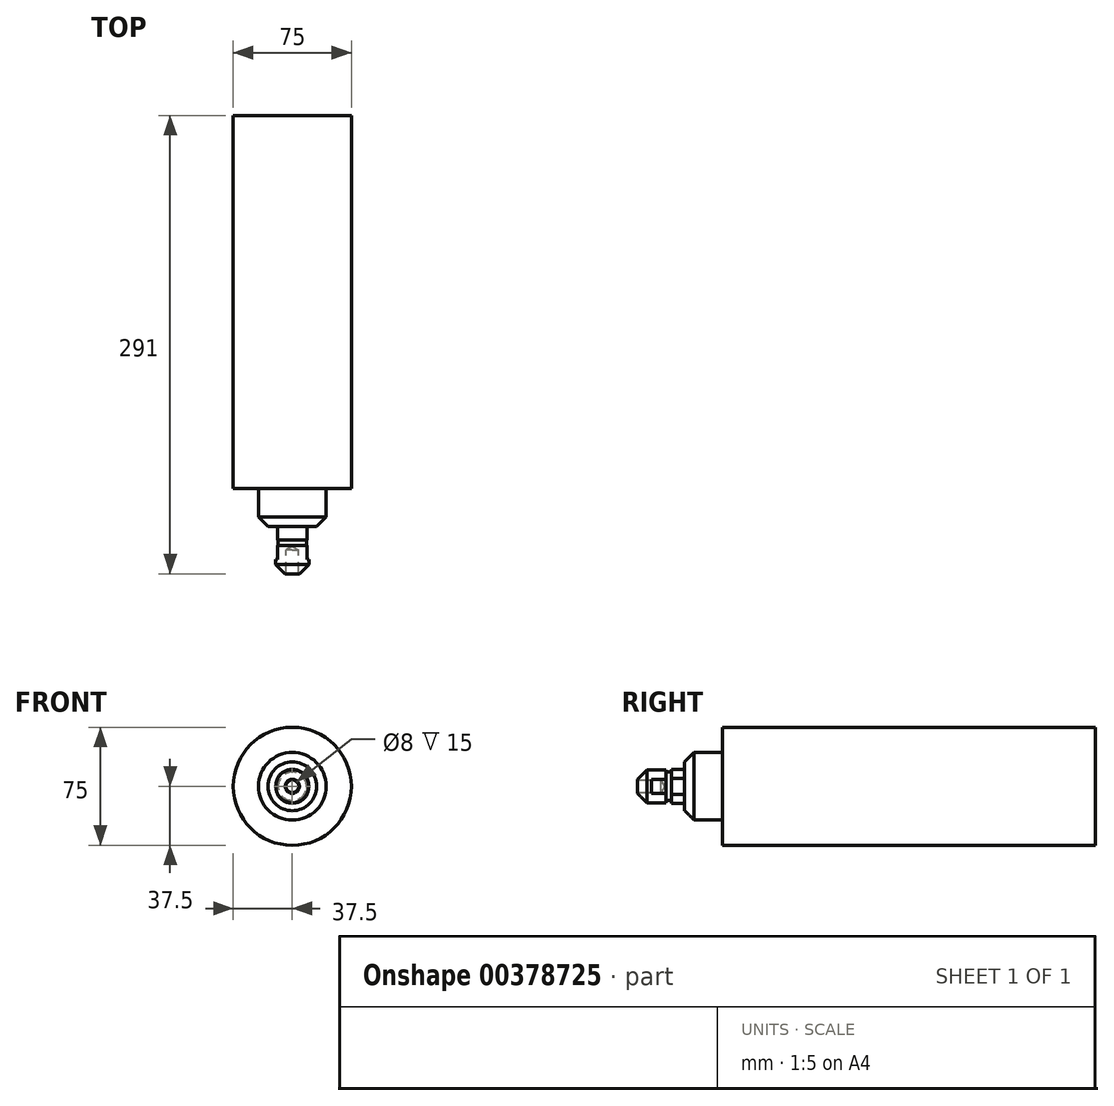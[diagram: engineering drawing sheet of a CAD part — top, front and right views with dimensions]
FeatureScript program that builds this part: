
annotation { "Feature Type Name" : "Feature", "Feature Type Description" : "" }
export const myFeature = defineFeature(function(context is Context, id is Id, definition is map)
    precondition{}
    {
        {
            var Q0;
            Q0=qCreatedBy(makeId("Right.planeOp"),FACE);
            var sketch = newSketch(context, id + "F0", { "sketchPlane" : qUnion([Q0])});
            skLineSegment(sketch, "E0", {"start": v(-61.56, 0) * mm, "end": v(-61.56, 4.5) * mm});
            skLineSegment(sketch, "E1", {"start": v(-61.56, 4.5) * mm, "end": v(-55.56, 10.5) * mm});
            skLineSegment(sketch, "E2", {"start": v(-55.56, 10.5) * mm, "end": v(-43.56, 10.5) * mm});
            skLineSegment(sketch, "E3", {"start": v(-43.56, 10.5) * mm, "end": v(-43.56, 9) * mm});
            skLineSegment(sketch, "E4", {"start": v(-43.56, 9) * mm, "end": v(-40.06, 9) * mm});
            skLineSegment(sketch, "E5", {"start": v(-31.56, 10.75) * mm, "end": v(-31.56, 15.5) * mm});
            skLineSegment(sketch, "E6", {"start": v(-25.56, 21.5) * mm, "end": v(-7.56, 21.5) * mm});
            skLineSegment(sketch, "E7", {"start": v(-7.56, 21.5) * mm, "end": v(-7.56, 37.5) * mm});
            skLineSegment(sketch, "E8", {"start": v(-7.56, 37.5) * mm, "end": v(229.44, 37.5) * mm});
            skLineSegment(sketch, "E9", {"start": v(229.44, 37.5) * mm, "end": v(229.44, 0) * mm});
            skLineSegment(sketch, "E10.MirrorCS", {"start": v(229.44, -37.5) * mm, "end": v(229.44, 0) * mm, "construction": true});
            skLineSegment(sketch, "E11.MirrorCS", {"start": v(-7.56, -37.5) * mm, "end": v(229.44, -37.5) * mm, "construction": true});
            skLineSegment(sketch, "E12.MirrorCS", {"start": v(-7.56, -21.5) * mm, "end": v(-7.56, -37.5) * mm, "construction": true});
            skLineSegment(sketch, "E13.MirrorCS", {"start": v(-31.56, -21.5) * mm, "end": v(-7.56, -21.5) * mm, "construction": true});
            skLineSegment(sketch, "E14.MirrorCS", {"start": v(-31.56, -10.75) * mm, "end": v(-31.56, -21.5) * mm, "construction": true});
            skLineSegment(sketch, "E15.MirrorCS", {"start": v(-43.56, -9) * mm, "end": v(-40.06, -9) * mm, "construction": true});
            skLineSegment(sketch, "E16.MirrorCS", {"start": v(-43.56, -10.5) * mm, "end": v(-43.56, -9) * mm, "construction": true});
            skLineSegment(sketch, "E17.MirrorCS", {"start": v(-55.56, -10.5) * mm, "end": v(-43.56, -10.5) * mm, "construction": true});
            skLineSegment(sketch, "E18.MirrorCS", {"start": v(-61.56, 0) * mm, "end": v(-61.56, -4.5) * mm, "construction": true});
            skLineSegment(sketch, "E19.MirrorCS", {"start": v(-61.56, -4.5) * mm, "end": v(-55.56, -10.5) * mm, "construction": true});
            skLineSegment(sketch, "E20", {"start": v(-61.56, 0) * mm, "end": v(229.44, 0) * mm, "construction": true});
            skLineSegment(sketch, "E21", {"start": v(-61.56, 0) * mm, "end": v(229.44, 0) * mm});
            skLineSegment(sketch, "E22", {"start": v(-40.06, 9) * mm, "end": v(-40.06, 10.75) * mm});
            skLineSegment(sketch, "E23", {"start": v(-40.06, 10.75) * mm, "end": v(-31.56, 10.75) * mm});
            skLineSegment(sketch, "E24", {"start": v(-40.06, -9) * mm, "end": v(-40.06, -10.75) * mm, "construction": true});
            skLineSegment(sketch, "E25", {"start": v(-40.06, -10.75) * mm, "end": v(-31.56, -10.75) * mm, "construction": true});
            skLineSegment(sketch, "E26", {"start": v(-31.56, 15.5) * mm, "end": v(-25.56, 21.5) * mm});
            skSolve(sketch);
        }
        {
            var Q0;
            Q0 = qSketchRegion(id + "F0", true);
            var Q1;
            Q1=sQuery(id+"F0.wireOp",EDGE,"E20");
            revolve(context, id + "F1", {"entities" : qUnion([Q0]), "axis" : qUnion([Q1]), "revolveType" : RevolveType.FULL});
        }
        {
            var Q0;
            Q0=makeQuery(id+"F1.opRevolve","SWEPT_FACE",FACE,{"disambiguationData":[OSD([sQuery(id+"F0.wireOp",EDGE,"E0")])]});
            var sketch = newSketch(context, id + "F2", { "sketchPlane" : qUnion([Q0])});
            skPoint(sketch, "E27", {"position": v(0, 0) * mm});
            skSolve(sketch);
        }
        {
            var Q0;
            Q0=sQuery(id+"F2.wireOp",VERTEX,"E27");
            var Q1;
            Q1=makeQuery(id+"F1.opRevolve","SWEPT_BODY",BODY,{"disambiguationData":[OSD([sQuery(id+"F0.wireOp",EDGE,"E0"),sQuery(id+"F0.wireOp",EDGE,"E1"),sQuery(id+"F0.wireOp",EDGE,"E2"),sQuery(id+"F0.wireOp",EDGE,"E3"),sQuery(id+"F0.wireOp",EDGE,"E4"),sQuery(id+"F0.wireOp",EDGE,"E5"),sQuery(id+"F0.wireOp",EDGE,"E6"),sQuery(id+"F0.wireOp",EDGE,"E7"),sQuery(id+"F0.wireOp",EDGE,"E8"),sQuery(id+"F0.wireOp",EDGE,"E9"),sQuery(id+"F0.wireOp",EDGE,"E21"),sQuery(id+"F0.wireOp",EDGE,"E22"),sQuery(id+"F0.wireOp",EDGE,"E23")])]});
            hole(context, id + "F3", {"style" : HoleStyle.SIMPLE, "endStyle" : HoleEndStyle.BLIND, "holeDiameter" : 8 * mm, "holeDepth" : 15 * mm, "isTappedThrough" : true, "tappedDepth" : 12 * mm, "tapClearance" : 3, "locations" : qUnion([Q0]), "scope" : qUnion([Q1]), "startStyle" : HoleStartStyle.PART});
        }
        {
            var Q0;
            Q0=qCreatedBy(makeId("Top.planeOp"),FACE);
            var sketch = newSketch(context, id + "F4", { "sketchPlane" : qUnion([Q0])});
            skLineSegment(sketch, "E28.bottom", {"start": v(9.5, -31.56) * mm, "end": v(12.5, -31.56) * mm});
            skLineSegment(sketch, "E28.top", {"start": v(9.5, -52.56) * mm, "end": v(12.5, -52.56) * mm});
            skLineSegment(sketch, "E28.left", {"start": v(9.5, -31.56) * mm, "end": v(9.5, -52.56) * mm});
            skLineSegment(sketch, "E28.right", {"start": v(12.5, -31.56) * mm, "end": v(12.5, -52.56) * mm});
            skLineSegment(sketch, "E29.MirrorCS", {"start": v(-9.5, -31.56) * mm, "end": v(-9.5, -52.56) * mm});
            skLineSegment(sketch, "E30.MirrorCS", {"start": v(-9.5, -52.56) * mm, "end": v(-12.5, -52.56) * mm});
            skLineSegment(sketch, "E31.MirrorCS", {"start": v(-12.5, -31.56) * mm, "end": v(-12.5, -52.56) * mm});
            skLineSegment(sketch, "E32.MirrorCS", {"start": v(-9.5, -31.56) * mm, "end": v(-12.5, -31.56) * mm});
            skSolve(sketch);
        }
        {
            var Q0;
            Q0 = qSketchRegion(id + "F4", true);
            extrude(context, id + "F5", {"entities" : qUnion([Q0]), "operationType" : NewBodyOperationType.REMOVE, "depth" : 25 * mm, "symmetric" : true});
        }
    });
